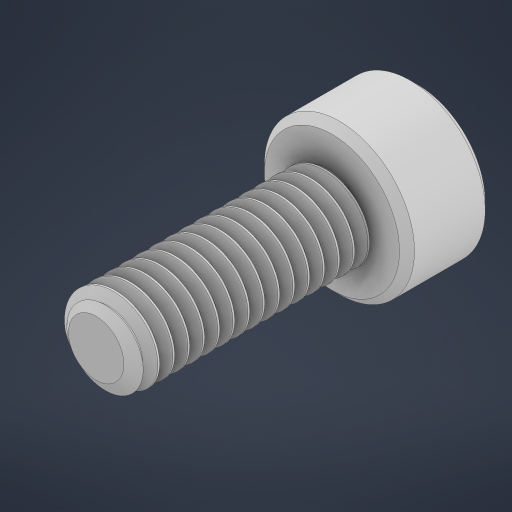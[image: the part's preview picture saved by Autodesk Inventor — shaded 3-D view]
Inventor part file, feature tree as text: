
AUTODESK INVENTOR PART (.ipt)
format: ipt  version: 2023 (Build 270158000, 158)  size: 695,296 bytes
history: native  units: in
note: dims shown in document units (in); Inventor stores cm internally (conversion verified against a paired STEP export)
features: chamfer x1
ambient origin geometry x8: Origin, YZ Plane, XZ Plane, XY Plane, X Axis, Y Axis, Z Axis, Center Point
bodies: Solid1 (feature_tree)
feature tree (1):
  chamfer  "Chamfer1"  [1 undecoded]
note: 1 required parameter value undecoded (feature->parameter linkage not recoverable at this tier; creation-order binding heuristic only, values carry confidence <= 0.55)
